# Revit family: ConcealedCistern-ForSquattingPans-8cm-VitrA-768-1700
name_source: partatom
category: Plumbing Fixtures
revit_build: Autodesk Revit 2017 (Build: 20160225_1515(x64)
units: mm (PartAtom-declared; Revit-internal decimal feet)

## family parameters
Cut with Voids When Loaded = No
Host = Face
OmniClass Number = 23.45.00.00
OmniClass Title = Sanitary, Laundry, and Cleaning Equipment
Part Type = Normal
Room Calculation Point = No
Round Connector Dimension = Use Diameter
Shared = Yes

## types (1)
- ConcealedCistern-ForSquattingPans-3/6lt-8cm-VitrA-768-1700-01
    Article No. (default) = 768-1700-01
    BIMobject category = Toilet Cisterns
    Brand = Vitra
    CW Connection = Yes
    Coating Material = Console
    Default Elevation = 1000 mm
    Description = VitrA Concealed Cistern for squatting pans - Standart Installation Set - Adjusted to 3/6 L
    Design country = Turkey
    HW Connection = No
    IFC Classification = Sanitary Terminal
    Manufacturer = Vitra
    Manufacturer name = Vitra
    Model = 768-1700-01
    Mounting type = Wall Mounted
    NBS Referans Code = 35-93-90
    NBS Referans Description = Wc Cisterns
    Nominal Depth (mm) = 80 mm  [stored 0.262467 ft]
    Nominal Height (mm) = 520 mm
    Nominal Width (mm) = 480 mm  [stored 1.5748 ft]
    OmniClass Code = 23-31 19 19
    OmniClass Description = Water Closets
    Primary Material = Orange
    Product Properties = Concealed Cistern for squatting pans - Standart Installation Set - Adjusted to 3/6 L
    Product SKU = 768-1700-01
    Product Type = Concealed Cistern
    Product certification = https://www.vitraglobal.com
    Product family = Vitra
    Product group = Concealed Cistern for squatting pans
    Product url = https://www.vitra.com.tr
    Secondary Material = White
    Technical description = https://www.vitra.com.tr
    Third Material = Blue
    URL = https://www.vitra.com.tr
    Uniclass 2.0 Code = PR-35-93-90
    Uniclass 2.0 Description = Wc Cisterns
    Uniclass 2015 Code = Pr_40_20_93_89
    Uniclass 2015 Name = WC cisterns
    Vent Connection = No
    Warranty Period (Year) = 10 Years
    Waste Connection = No
    Weight Net (kg) = 4.4
    Youtube = https://www.youtube.com

note: [stored X ft] marks values corroborated as IEEE doubles in the binary element streams (Revit-internal decimal feet)

## geometry (parser evidence)
native form markers: Sweep x1
no freeform markers — native parametric forms only
